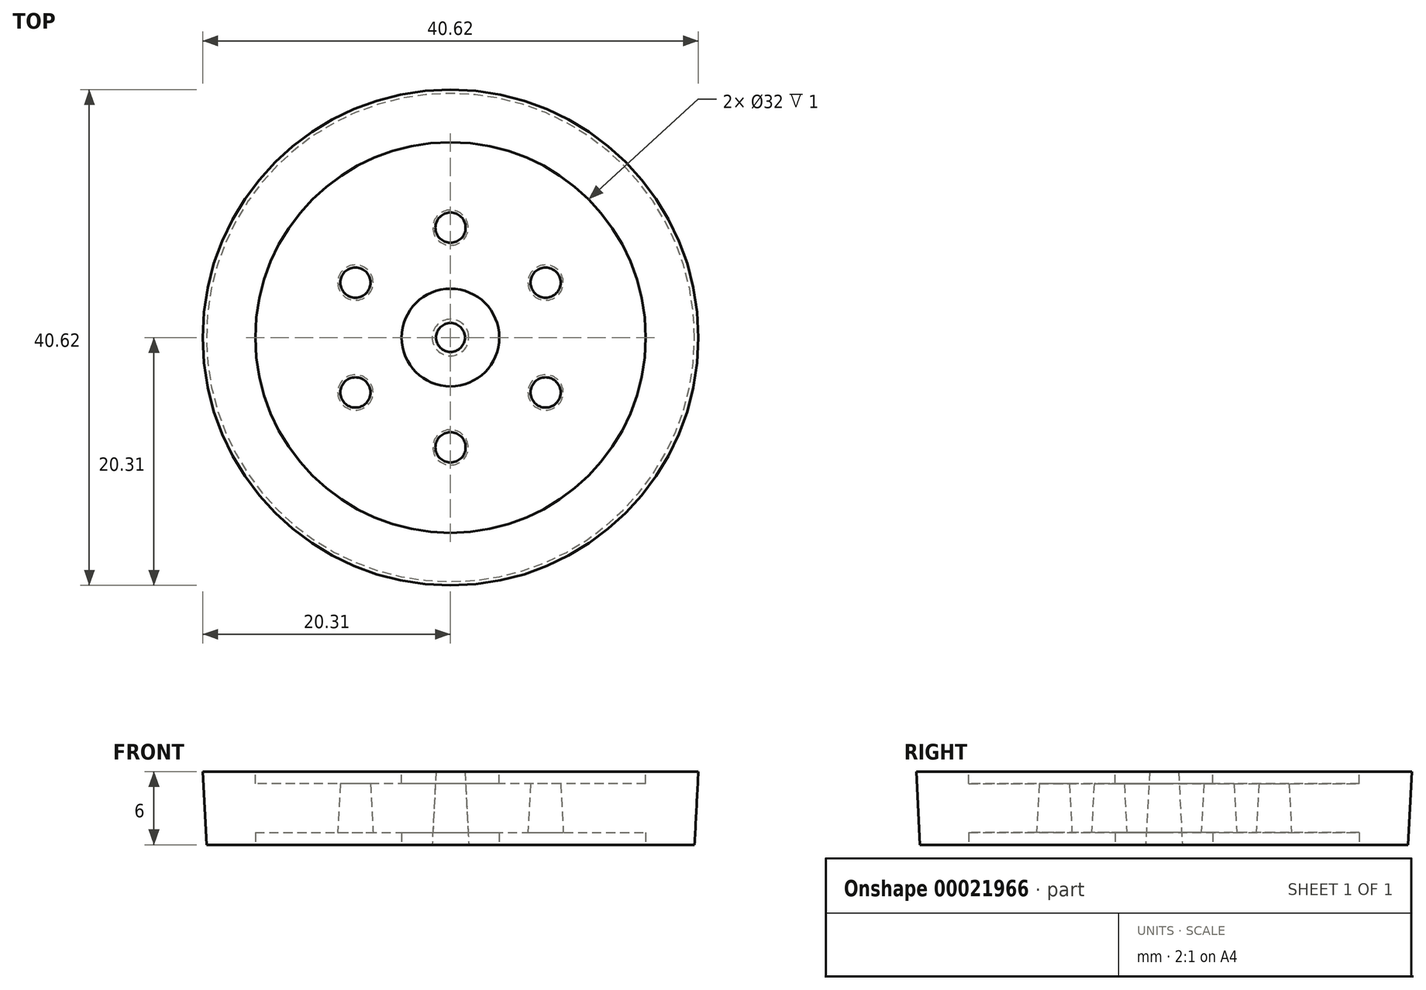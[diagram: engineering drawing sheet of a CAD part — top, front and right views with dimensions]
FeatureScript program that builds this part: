
annotation { "Feature Type Name" : "Feature", "Feature Type Description" : "" }
export const myFeature = defineFeature(function(context is Context, id is Id, definition is map)
    precondition{}
    {
        {
            var Q0;
            Q0=qCreatedBy(makeId("Top.planeOp"),FACE);
            var sketch = newSketch(context, id + "F0", { "sketchPlane" : qUnion([Q0])});
            skCircle(sketch, "E0", {"center": v(0, 0) * mm, "radius": 20 * mm});
            skCircle(sketch, "E1", {"center": v(0, 0) * mm, "radius": 1.5 * mm});
            skCircle(sketch, "E2", {"center": v(0, 9) * mm, "radius": 1.5 * mm});
            skArc(sketch, "E3", {"start": v(-6.94, 5.73) * mm, "mid": v(-7.8, 4.5) * mm, "end": v(-8.43, 3.14) * mm});
            skArc(sketch, "E4.cCircle", {"start": v(-6.94, 5.73) * mm, "mid": v(-7.8, 4.5) * mm, "end": v(-8.43, 3.14) * mm, "construction": true});
            skLineSegment(sketch, "E4.0", {"start": v(0, 9) * mm, "end": v(1.3, 8.25) * mm});
            skLineSegment(sketch, "E4.1", {"start": v(7.8, 4.5) * mm, "end": v(7.8, 3) * mm});
            skLineSegment(sketch, "E4.2", {"start": v(7.8, -4.5) * mm, "end": v(6.5, -5.25) * mm});
            skLineSegment(sketch, "E4.3", {"start": v(0, -9) * mm, "end": v(-1.3, -8.25) * mm});
            skLineSegment(sketch, "E4.4", {"start": v(-7.8, -4.5) * mm, "end": v(-7.8, -3) * mm});
            skLineSegment(sketch, "E4.5", {"start": v(-7.8, 4.5) * mm, "end": v(-6.5, 5.25) * mm});
            skCircle(sketch, "E5", {"center": v(7.8, 4.5) * mm, "radius": 1.5 * mm});
            skCircle(sketch, "E6", {"center": v(7.8, -4.5) * mm, "radius": 1.5 * mm});
            skCircle(sketch, "E7", {"center": v(0, -9) * mm, "radius": 1.5 * mm});
            skCircle(sketch, "E8", {"center": v(-7.8, -4.5) * mm, "radius": 1.5 * mm});
            skCircle(sketch, "E9", {"center": v(-7.8, 4.5) * mm, "radius": 1.5 * mm});
            skLineSegment(sketch, "E10.trimOffspring", {"start": v(-1.3, 8.25) * mm, "end": v(0, 9) * mm});
            skArc(sketch, "E11.trimOffspring", {"start": v(1.5, 8.88) * mm, "mid": v(0, 9) * mm, "end": v(-1.5, 8.88) * mm});
            skLineSegment(sketch, "E12.trimOffspring", {"start": v(6.5, 5.25) * mm, "end": v(7.8, 4.5) * mm});
            skArc(sketch, "E13.trimOffspring", {"start": v(1.5, 8.88) * mm, "mid": v(0, 9) * mm, "end": v(-1.5, 8.88) * mm, "construction": true});
            skArc(sketch, "E14.trimOffspring", {"start": v(8.43, 3.14) * mm, "mid": v(7.8, 4.5) * mm, "end": v(6.94, 5.73) * mm});
            skArc(sketch, "E15.trimOffspring", {"start": v(8.43, 3.14) * mm, "mid": v(7.8, 4.5) * mm, "end": v(6.94, 5.73) * mm, "construction": true});
            skLineSegment(sketch, "E16.trimOffspring", {"start": v(7.8, -3) * mm, "end": v(7.8, -4.5) * mm});
            skLineSegment(sketch, "E17.trimOffspring", {"start": v(1.3, -8.25) * mm, "end": v(0, -9) * mm});
            skArc(sketch, "E18.trimOffspring", {"start": v(6.94, -5.73) * mm, "mid": v(7.8, -4.5) * mm, "end": v(8.43, -3.14) * mm});
            skArc(sketch, "E19.trimOffspring", {"start": v(6.94, -5.73) * mm, "mid": v(7.8, -4.5) * mm, "end": v(8.43, -3.14) * mm, "construction": true});
            skArc(sketch, "E20.trimOffspring", {"start": v(-1.5, -8.88) * mm, "mid": v(0, -9) * mm, "end": v(1.5, -8.88) * mm});
            skArc(sketch, "E21.trimOffspring", {"start": v(-1.5, -8.88) * mm, "mid": v(0, -9) * mm, "end": v(1.5, -8.88) * mm, "construction": true});
            skLineSegment(sketch, "E22.trimOffspring", {"start": v(-6.5, -5.25) * mm, "end": v(-7.8, -4.5) * mm});
            skLineSegment(sketch, "E23.trimOffspring", {"start": v(-7.8, 3) * mm, "end": v(-7.8, 4.5) * mm});
            skArc(sketch, "E24.trimOffspring", {"start": v(-8.43, -3.14) * mm, "mid": v(-7.8, -4.5) * mm, "end": v(-6.94, -5.73) * mm});
            skArc(sketch, "E25.trimOffspring", {"start": v(-8.43, -3.14) * mm, "mid": v(-7.8, -4.5) * mm, "end": v(-6.94, -5.73) * mm, "construction": true});
            skSolve(sketch);
        }
        {
            var Q0;
            Q0=makeQuery(id+"F0.imprint","IMPRINT",FACE,{"disambiguationData":[TD([[makeQuery(id+"F0.imprint","IMPRINT",EDGE,{"derivedFrom":sQuery(id+"F0.wireOp",EDGE,"E0")}),1.0]])]});
            extrude(context, id + "F1", {"entities" : qUnion([Q0]), "depth" : 6 * mm, "hasDraft" : true, "draftAngle" : 3 * degree});
        }
        {
            var Q0;
            Q0=makeQuery(id+"F1.opExtrude","CAP_FACE",FACE,{"disambiguationData":[OSD([sQuery(id+"F0.wireOp",EDGE,"E0"),sQuery(id+"F0.wireOp",EDGE,"E1"),sQuery(id+"F0.wireOp",EDGE,"E2"),sQuery(id+"F0.wireOp",EDGE,"E5"),sQuery(id+"F0.wireOp",EDGE,"E6"),sQuery(id+"F0.wireOp",EDGE,"E7"),sQuery(id+"F0.wireOp",EDGE,"E8"),sQuery(id+"F0.wireOp",EDGE,"E9")])],"isStart":false});
            var sketch = newSketch(context, id + "F2", { "sketchPlane" : qUnion([Q0])});
            skCircle(sketch, "E26", {"center": v(0, 0) * mm, "radius": 16 * mm});
            skCircle(sketch, "E27", {"center": v(0, 0) * mm, "radius": 4 * mm});
            skSolve(sketch);
        }
        {
            var Q0;
            Q0=makeQuery(id+"F2.imprint","IMPRINT",FACE,{"disambiguationData":[TD([[makeQuery(id+"F2.imprint","IMPRINT",EDGE,{"derivedFrom":sQuery(id+"F2.wireOp",EDGE,"E26")}),1.0]])]});
            extrude(context, id + "F3", {"entities" : qUnion([Q0]), "operationType" : NewBodyOperationType.REMOVE, "oppositeDirection" : true, "depth" : 1 * mm});
        }
        {
            var Q0;
            Q0=makeQuery(id+"F1.opExtrude","CAP_FACE",FACE,{"disambiguationData":[OSD([sQuery(id+"F0.wireOp",EDGE,"E0"),sQuery(id+"F0.wireOp",EDGE,"E1"),sQuery(id+"F0.wireOp",EDGE,"E2"),sQuery(id+"F0.wireOp",EDGE,"E5"),sQuery(id+"F0.wireOp",EDGE,"E6"),sQuery(id+"F0.wireOp",EDGE,"E7"),sQuery(id+"F0.wireOp",EDGE,"E8"),sQuery(id+"F0.wireOp",EDGE,"E9")])],"isStart":true});
            var sketch = newSketch(context, id + "F4", { "sketchPlane" : qUnion([Q0])});
            skCircle(sketch, "E28", {"center": v(0, 0) * mm, "radius": 4 * mm});
            skCircle(sketch, "E29", {"center": v(0, 0) * mm, "radius": 16 * mm});
            skSolve(sketch);
        }
        {
            var Q0;
            Q0 = qSketchRegion(id + "F4", true);
            var Q1;
            Q1=makeQuery(id+"F4.imprint","IMPRINT",FACE,{"disambiguationData":[TD([[makeQuery(id+"F4.imprint","IMPRINT",EDGE,{"derivedFrom":sQuery(id+"F4.wireOp",EDGE,"E28")}),-1.0]])]});
            extrude(context, id + "F5", {"entities" : qUnion([Q0, Q1]), "operationType" : NewBodyOperationType.REMOVE, "oppositeDirection" : true, "depth" : 1 * mm});
        }
    });
